# Revit family: Haworth_Pergola_Drapery_Straight
name_source: partatom
category: Furniture Systems
revit_build: Autodesk Revit 2018 (Build: 20170223_1515(x64)
units: mm (PartAtom-declared; Revit-internal decimal feet)

## family parameters
Always vertical = Yes
Cut with Voids When Loaded = No
OmniClass Number = 23.40.70.14.64.21
OmniClass Title = Systems Furniture
Part Type = Normal
Room Calculation Point = No
Round Connector Dimension = Use Diameter
Shared = No
Work Plane-Based = No

## types (10) — shared parameters
Actual Depth = 4"
Actual Height = 91 1/4"
Assembly Code = E2020200
Base Height = 1 1/2"
Bracket Thickness = 25/128"
Custom Size = No
Description = Haworth - Pergola Drapery - Straight
End Slat Offset = 4"
Manufacturer = Haworth
Max. Height = 89 1/2"
Max. Width = 144"
Min. Height = 89 1/2"
Min. Width = 48"
Model = Haworth Pergola
Revision Number = 1
Size = Verify Final Dim. w/ Haworth
Standard Width = 48, 72, 96, 120, 144 in.
Sustainability Info = http://www.haworth.com
Trim Finish = Haworth _ Paint _ Undecided _ Pergola
URL = http://www.haworth.com
URL - Product = https://www.haworth.com
Warranty = http://www.haworth.com

## per-type parameters (varying)
| type | 120in Wide Drapery | 144in Wide Drapery | 24in Wide Drapery - Left | 24in Wide Drapery - Right | 36in Wide Drapery - Left | 36in Wide Drapery - Right | 48in Wide Drapery | 72in Wide Drapery | 96in Wide Drapery | Actual Width | Closed Drapery | Curtain Finish | Half Open Drapery | Slat Count | Top Drapery Offset | Width |
| 144w - Half Open Drapery | No | No | No | No | Yes | Yes | No | No | No | 144" | No | Haworth _ Fabric _ Undecided _ Pergola | Yes | 18 | 0" | 144" |
| 72w - Half Open Drapery | No | No | No | No | Yes | No | No | No | No | 72" | No | Haworth _ Paint _ Undecided _ Pergola | Yes | 9 | 1/2" | 72" |
| 48w - Half Open Drapery | No | No | Yes | No | No | No | No | No | No | 48" | No | Haworth _ Paint _ Undecided _ Pergola | Yes | 6 | 1/2" | 48" |
| 96w - Half Open Drapery | No | No | No | No | No | No | Yes | No | No | 96" | No | Haworth _ Paint _ Undecided _ Pergola | Yes | 12 | 1/2" | 96" |
| 120w - Half Open Drapery | No | No | Yes | Yes | No | No | No | No | No | 120" | No | Haworth _ Paint _ Undecided _ Pergola | Yes | 15 | 1/2" | 120" |
| 120w - Closed Drapery | Yes | No | No | No | No | No | No | No | No | 120" | Yes | Haworth _ Paint _ Undecided _ Pergola | No | 15 | 1/2" | 120" |
| 144w - Closed Drapery | No | Yes | No | No | No | No | No | No | No | 144" | Yes | Haworth _ Fabric _ Undecided _ Pergola | No | 18 | 1/2" | 144" |
| 48w - Closed Drapery | No | No | No | No | No | No | Yes | No | No | 48" | Yes | Haworth _ Paint _ Undecided _ Pergola | No | 6 | 1/2" | 48" |
| 72w - Closed Drapery | No | No | No | No | No | No | No | Yes | No | 72" | Yes | Haworth _ Paint _ Undecided _ Pergola | No | 9 | 1/2" | 72" |
| 96w - Closed Drapery | No | No | No | No | No | No | No | No | Yes | 96" | Yes | Haworth _ Paint _ Undecided _ Pergola | No | 12 | 1/2" | 96" |

## geometry (parser evidence)
native form markers: Sweep x5
no freeform markers — native parametric forms only
